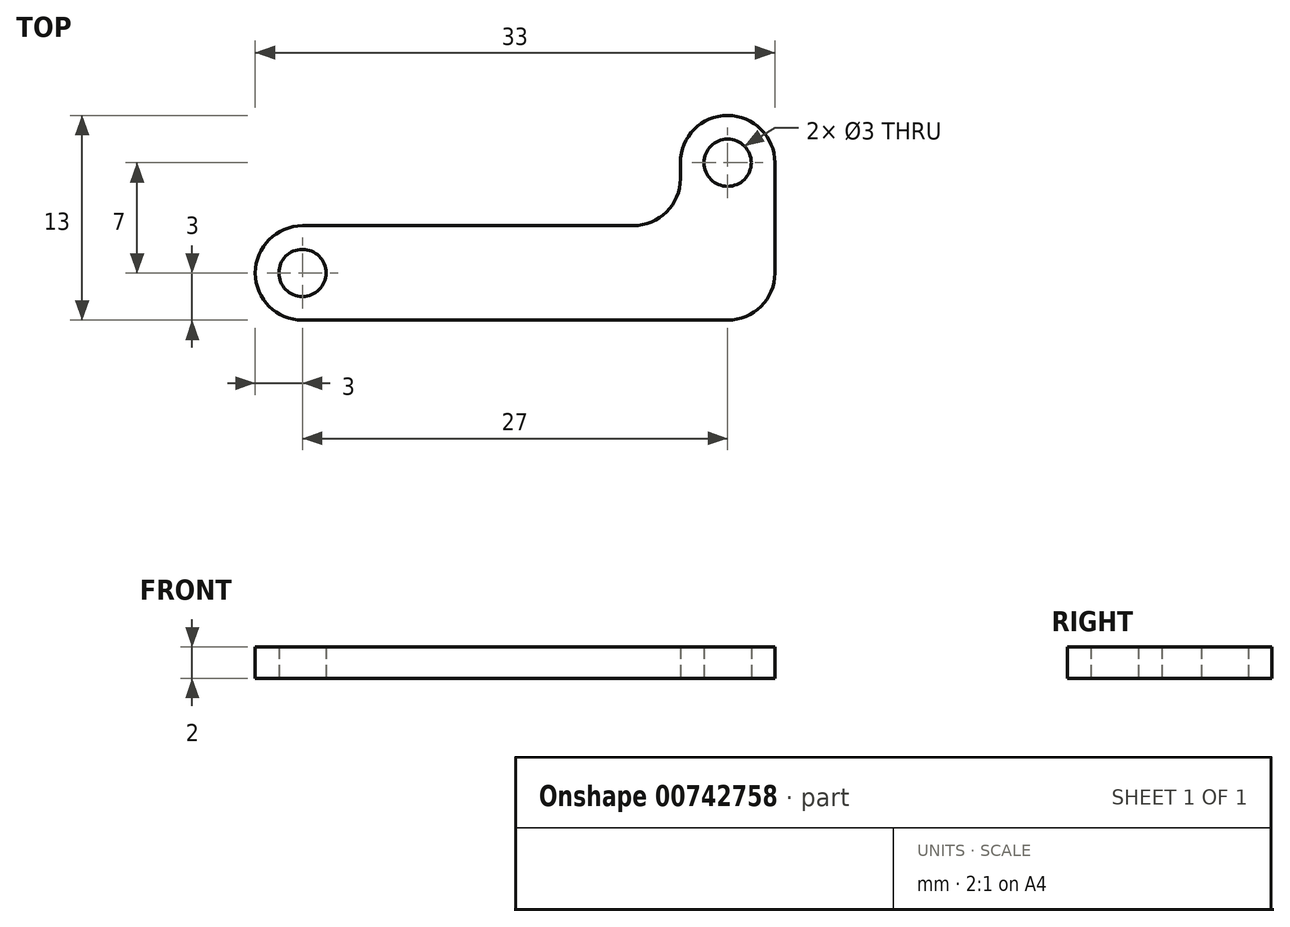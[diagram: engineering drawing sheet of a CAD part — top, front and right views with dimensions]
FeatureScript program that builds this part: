
annotation { "Feature Type Name" : "Feature", "Feature Type Description" : "" }
export const myFeature = defineFeature(function(context is Context, id is Id, definition is map)
    precondition{}
    {
        {
            var Q0;
            Q0=qCreatedBy(makeId("Top.planeOp"),FACE);
            var sketch = newSketch(context, id + "F0", { "sketchPlane" : qUnion([Q0])});
            skLineSegment(sketch, "E0.left", {"start": v(0, 0) * mm, "end": v(0, 10) * mm});
            skLineSegment(sketch, "E0.right", {"start": v(-6, 9) * mm, "end": v(-6, 10) * mm});
            skLineSegment(sketch, "E1.bottom", {"start": v(-3, 0) * mm, "end": v(-30, 0) * mm});
            skLineSegment(sketch, "E1.top", {"start": v(-9, 6) * mm, "end": v(-30, 6) * mm});
            skLineSegment(sketch, "E1.left", {"start": v(0, 3) * mm, "end": v(0, 6) * mm});
            skArc(sketch, "E2", {"start": v(0, 10) * mm, "mid": v(-3, 13) * mm, "end": v(-6, 10) * mm});
            skArc(sketch, "E3", {"start": v(-30, 6) * mm, "mid": v(-33, 3) * mm, "end": v(-30, 0) * mm});
            skPoint(sketch, "E4.visualSharp", {"position": v(-6, 6) * mm});
            skArc(sketch, "E4.filletArc", {"start": v(-9, 6) * mm, "mid": v(-6.88, 6.88) * mm, "end": v(-6, 9) * mm});
            skPoint(sketch, "E5.visualSharp", {"position": v(0, 0) * mm});
            skArc(sketch, "E5.filletArc", {"start": v(-3, 0) * mm, "mid": v(-0.88, 0.88) * mm, "end": v(0, 3) * mm});
            skCircle(sketch, "E6", {"center": v(-30, 3) * mm, "radius": 1.5 * mm});
            skCircle(sketch, "E7", {"center": v(-3, 10) * mm, "radius": 1.5 * mm});
            skSolve(sketch);
        }
        {
            var Q0;
            Q0 = qSketchRegion(id + "F0", true);
            extrude(context, id + "F1", {"entities" : qUnion([Q0]), "depth" : 2 * mm, "offsetDistance" : 25 * mm});
        }
    });
